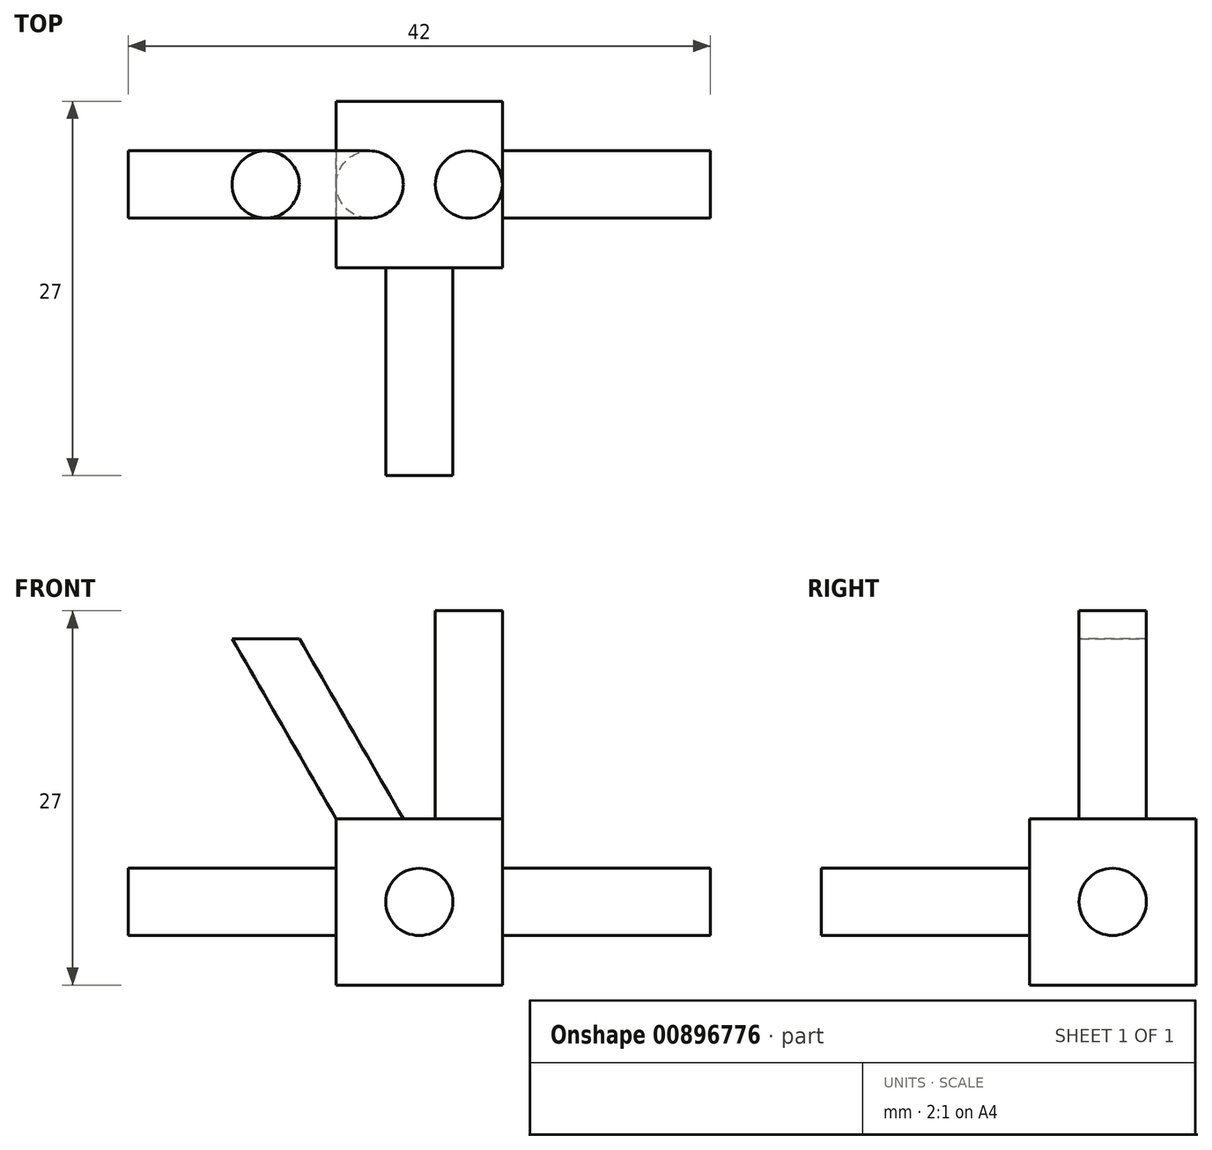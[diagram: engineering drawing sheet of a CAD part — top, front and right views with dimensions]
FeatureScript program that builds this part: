
annotation { "Feature Type Name" : "Feature", "Feature Type Description" : "" }
export const myFeature = defineFeature(function(context is Context, id is Id, definition is map)
    precondition{}
    {
        {
            var Q0;
            Q0=qCreatedBy(makeId("Top.planeOp"),FACE);
            var sketch = newSketch(context, id + "F0", { "sketchPlane" : qUnion([Q0])});
            skLineSegment(sketch, "E0", {"start": v(-22.31, 15.26) * mm, "end": v(-22.31, 3.26) * mm});
            skLineSegment(sketch, "E1", {"start": v(-22.31, 3.26) * mm, "end": v(-10.31, 3.26) * mm});
            skLineSegment(sketch, "E2", {"start": v(-10.31, 3.26) * mm, "end": v(-10.31, 15.26) * mm});
            skLineSegment(sketch, "E3", {"start": v(-10.31, 15.26) * mm, "end": v(-22.31, 15.26) * mm});
            skSolve(sketch);
        }
        {
            var Q0;
            Q0=qSketchRegion(id+"F0",true);
            extrude(context, id + "F1", {"entities" : qUnion([Q0]), "depth" : 12 * mm, "offsetDistance" : 25 * mm});
        }
        {
            var Q0;
            Q0=makeQuery(id+"F1.opExtrude","SWEPT_FACE",FACE,{"disambiguationData":[OSD([sQuery(id+"F0.wireOp",EDGE,"E2")])]});
            var sketch = newSketch(context, id + "F2", { "sketchPlane" : qUnion([Q0])});
            skCircle(sketch, "E4", {"center": v(9.26, 6) * mm, "radius": 2.43 * mm});
            skSolve(sketch);
        }
        {
            var Q0;
            Q0=makeQuery(id+"F2.imprint","IMPRINT",FACE,{"disambiguationData":[TD([[makeQuery(id+"F2.imprint","IMPRINT",EDGE,{"derivedFrom":sQuery(id+"F2.wireOp",EDGE,"E4")}),1.0]])]});
            extrude(context, id + "F3", {"entities" : qUnion([Q0]), "operationType" : NewBodyOperationType.ADD, "depth" : 15 * mm, "offsetDistance" : 25 * mm});
        }
        {
            var Q0;
            Q0=makeQuery(id+"F1.opExtrude","SWEPT_FACE",FACE,{"disambiguationData":[OSD([sQuery(id+"F0.wireOp",EDGE,"E0")])]});
            var sketch = newSketch(context, id + "F4", { "sketchPlane" : qUnion([Q0])});
            skCircle(sketch, "E5", {"center": v(-9.26, 6) * mm, "radius": 2.43 * mm});
            skSolve(sketch);
        }
        {
            var Q0;
            Q0=qSketchRegion(id+"F4",true);
            extrude(context, id + "F5", {"entities" : qUnion([Q0]), "operationType" : NewBodyOperationType.ADD, "depth" : 15 * mm, "offsetDistance" : 25 * mm});
        }
        {
            var Q0;
            Q0=makeQuery(id+"F1.opExtrude","SWEPT_FACE",FACE,{"disambiguationData":[OSD([sQuery(id+"F0.wireOp",EDGE,"E1")])]});
            var sketch = newSketch(context, id + "F6", { "sketchPlane" : qUnion([Q0])});
            skCircle(sketch, "E6", {"center": v(-16.31, 6) * mm, "radius": 2.43 * mm});
            skSolve(sketch);
        }
        {
            var Q0;
            Q0=qSketchRegion(id+"F6",true);
            extrude(context, id + "F7", {"entities" : qUnion([Q0]), "operationType" : NewBodyOperationType.ADD, "depth" : 15 * mm, "offsetDistance" : 25 * mm});
        }
        {
            var Q0;
            Q0=makeQuery(id+"F1.opExtrude","CAP_FACE",FACE,{"disambiguationData":[OSD([sQuery(id+"F0.wireOp",EDGE,"E0"),sQuery(id+"F0.wireOp",EDGE,"E1"),sQuery(id+"F0.wireOp",EDGE,"E2"),sQuery(id+"F0.wireOp",EDGE,"E3")])],"isStart":false});
            var sketch = newSketch(context, id + "F8", { "sketchPlane" : qUnion([Q0])});
            skCircle(sketch, "E7", {"center": v(-19.89, 9.26) * mm, "radius": 2.43 * mm});
            skCircle(sketch, "E8", {"center": v(-12.74, 9.26) * mm, "radius": 2.43 * mm});
            skSolve(sketch);
        }
        {
            var Q0;
            Q0=makeQuery(id+"F1.opExtrude","SWEPT_FACE",FACE,{"disambiguationData":[OSD([sQuery(id+"F0.wireOp",EDGE,"E3")])]});
            var sketch = newSketch(context, id + "F9", { "sketchPlane" : qUnion([Q0])});
            skPoint(sketch, "E9.0", {"position": v(12.74, 12) * mm});
            skPoint(sketch, "E10.0", {"position": v(19.89, 12) * mm});
            skLineSegment(sketch, "E11", {"start": v(19.89, 12) * mm, "end": v(27.39, 25) * mm});
            skSolve(sketch);
        }
        {
            var Q0;
            Q0=makeQuery(id+"F8.imprint","IMPRINT",FACE,{"disambiguationData":[TD([[makeQuery(id+"F8.imprint","IMPRINT",EDGE,{"derivedFrom":sQuery(id+"F8.wireOp",EDGE,"E7")}),1.0]])]});
            var Q1;
            Q1=sQuery(id+"F9.wireOp",EDGE,"E11");
            sweep(context, id + "F10", {"operationType" : NewBodyOperationType.ADD, "profiles" : qUnion([Q0]), "path" : qUnion([Q1])});
        }
        {
            var Q0;
            Q0 = qSketchRegion(id + "F9", true);
            var Q1;
            Q1=makeQuery(id+"F8.imprint","IMPRINT",FACE,{"disambiguationData":[TD([[makeQuery(id+"F8.imprint","IMPRINT",EDGE,{"derivedFrom":sQuery(id+"F8.wireOp",EDGE,"E8")}),1.0]])]});
            extrude(context, id + "F11", {"entities" : qUnion([Q0, Q1]), "operationType" : NewBodyOperationType.ADD, "depth" : 15 * mm, "offsetDistance" : 25 * mm});
        }
    });
